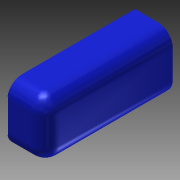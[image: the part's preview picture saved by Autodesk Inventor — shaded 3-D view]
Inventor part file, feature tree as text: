
AUTODESK INVENTOR PART (.ipt)
format: ipt  version: 2013 (Build 170138000, 138)  size: 182,272 bytes
history: native  units: in
note: dims shown in document units (in); Inventor stores cm internally (conversion verified against a paired STEP export)
features: reference x4, extrude x3, sketch x2, fillet x1, projected_geometry x1
ambient origin geometry x8: Origin, YZ Plane, XZ Plane, XY Plane, X Axis, Y Axis, Z Axis, Center Point
bodies: Solid1 (feature_tree)
feature tree (11):
  sketch  "Sketch1"  dims[d0=0.0625in d1=0.0in d3=1.0in]
  extrude  "Extrusion1"  Depth=1.0in
  extrude  "Extrusion2"  Depth=0.0625in
  extrude  "Extrusion3"  Depth=11.25in TaperAngle=0.0deg
  fillet  "Fillet1"  Radius=0.0625in
  reference  "Reference4"
  reference  "Reference5"
  sketch  "Sketch2"  dims[d7=1.0in d9=0.0625in d10=11.25in d11=0.0in d12=0.0625in d13=0.0in d14=1.3125in d15=0.0625in d16=0.0625in]
  reference  "Reference6"
  projected_geometry  "Projected Loop1"
  reference  "Reference7"
